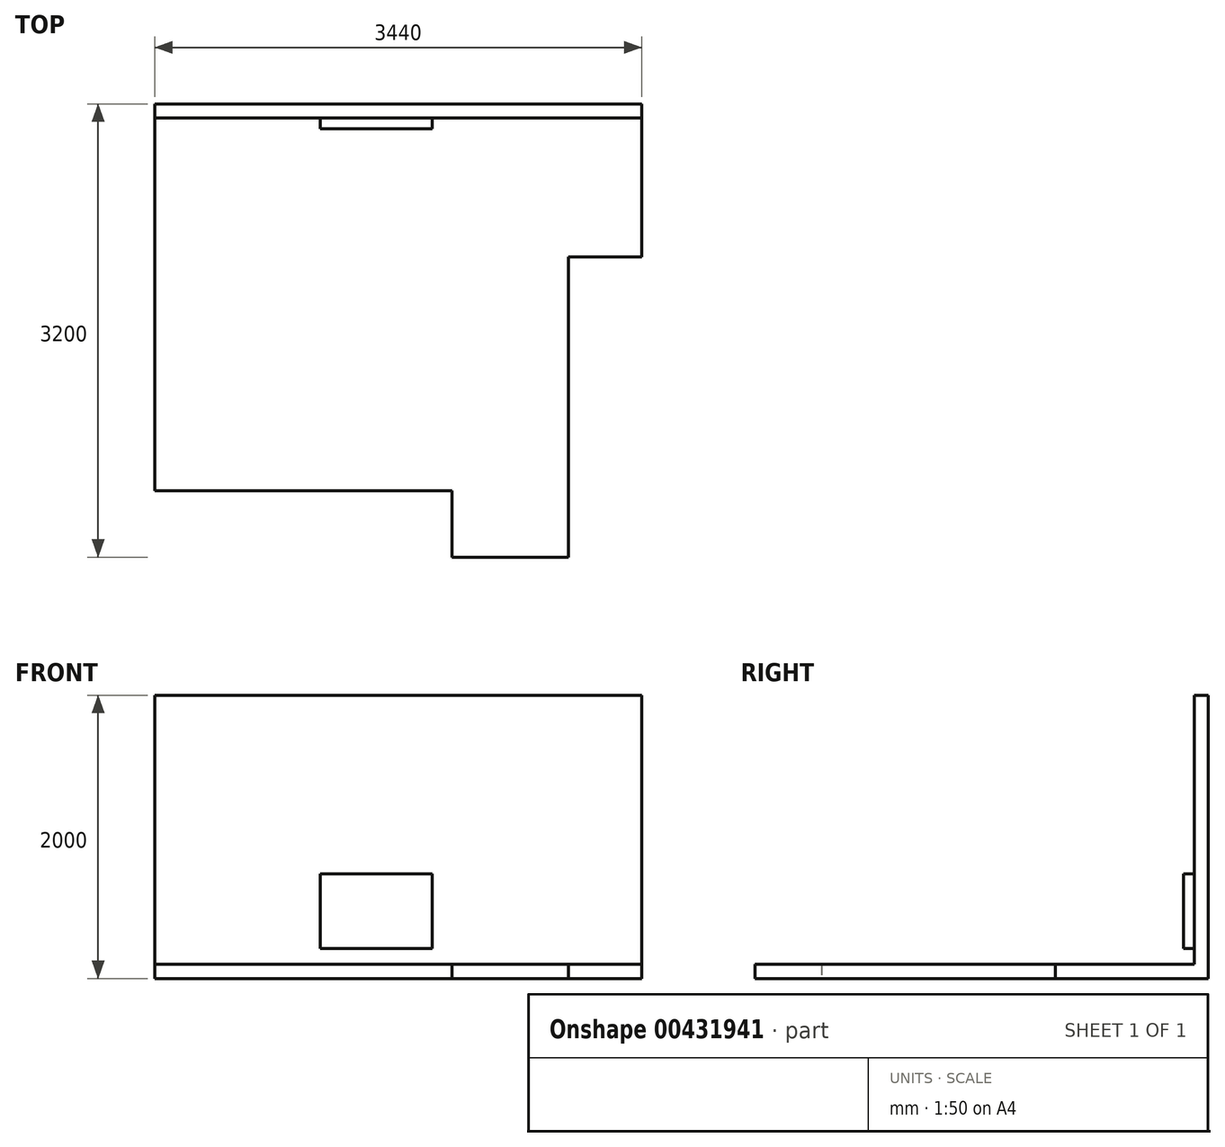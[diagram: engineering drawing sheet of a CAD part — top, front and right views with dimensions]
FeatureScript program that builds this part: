
annotation { "Feature Type Name" : "Feature", "Feature Type Description" : "" }
export const myFeature = defineFeature(function(context is Context, id is Id, definition is map)
    precondition{}
    {
        {
            var Q0;
            Q0=qCreatedBy(makeId("Top.planeOp"),FACE);
            var sketch = newSketch(context, id + "F0", { "sketchPlane" : qUnion([Q0])});
            skLineSegment(sketch, "E0.bottom", {"start": v(0, 0) * mm, "end": v(-820, 0) * mm});
            skLineSegment(sketch, "E0.left", {"start": v(0, 0) * mm, "end": v(0, 2120) * mm});
            skLineSegment(sketch, "E0.right", {"start": v(-820, 0) * mm, "end": v(-820, 470) * mm});
            skLineSegment(sketch, "E1.bottom", {"start": v(-820, 470) * mm, "end": v(-2920, 470) * mm});
            skLineSegment(sketch, "E1.top", {"start": v(520, 3100) * mm, "end": v(-2920, 3100) * mm});
            skLineSegment(sketch, "E1.right", {"start": v(-2920, 470) * mm, "end": v(-2920, 3100) * mm});
            skLineSegment(sketch, "E2.top", {"start": v(0, 2120) * mm, "end": v(520, 2120) * mm});
            skLineSegment(sketch, "E2.right", {"start": v(520, 3100) * mm, "end": v(520, 2120) * mm});
            skSolve(sketch);
        }
        {
            var Q0;
            Q0 = qSketchRegion(id + "F0", true);
            extrude(context, id + "F1", {"entities" : qUnion([Q0]), "depth" : 100 * mm});
        }
        {
            var Q0;
            Q0=makeQuery(id+"F1.opExtrude","SWEPT_FACE",FACE,{"disambiguationData":[OSD([sQuery(id+"F0.wireOp",EDGE,"E1.top")])]});
            var sketch = newSketch(context, id + "F2", { "sketchPlane" : qUnion([Q0])});
            skLineSegment(sketch, "E3.bottom", {"start": v(-520, 0) * mm, "end": v(2920, 0) * mm});
            skLineSegment(sketch, "E3.top", {"start": v(-520, 2000) * mm, "end": v(2920, 2000) * mm});
            skLineSegment(sketch, "E3.left", {"start": v(-520, 0) * mm, "end": v(-520, 2000) * mm});
            skLineSegment(sketch, "E3.right", {"start": v(2920, 0) * mm, "end": v(2920, 2000) * mm});
            skSolve(sketch);
        }
        {
            var Q0;
            Q0 = qSketchRegion(id + "F2", true);
            extrude(context, id + "F3", {"entities" : qUnion([Q0]), "operationType" : NewBodyOperationType.ADD, "depth" : 100 * mm});
        }
        {
            var Q0;
            Q0=makeQuery(id+"F3.opExtrude","CAP_FACE",FACE,{"disambiguationData":[OSD([sQuery(id+"F2.wireOp",EDGE,"E3.bottom"),sQuery(id+"F2.wireOp",EDGE,"E3.top"),sQuery(id+"F2.wireOp",EDGE,"E3.left"),sQuery(id+"F2.wireOp",EDGE,"E3.right")])],"isStart":true});
            var sketch = newSketch(context, id + "F4", { "sketchPlane" : qUnion([Q0])});
            skLineSegment(sketch, "E4.bottom", {"start": v(-1750, 210) * mm, "end": v(-960, 210) * mm});
            skLineSegment(sketch, "E4.top", {"start": v(-1750, 740) * mm, "end": v(-960, 740) * mm});
            skLineSegment(sketch, "E4.left", {"start": v(-1750, 210) * mm, "end": v(-1750, 740) * mm});
            skLineSegment(sketch, "E4.right", {"start": v(-960, 210) * mm, "end": v(-960, 740) * mm});
            skSolve(sketch);
        }
        {
            var Q0;
            Q0 = qSketchRegion(id + "F4", true);
            extrude(context, id + "F5", {"entities" : qUnion([Q0]), "operationType" : NewBodyOperationType.ADD, "depth" : 75 * mm});
        }
    });
